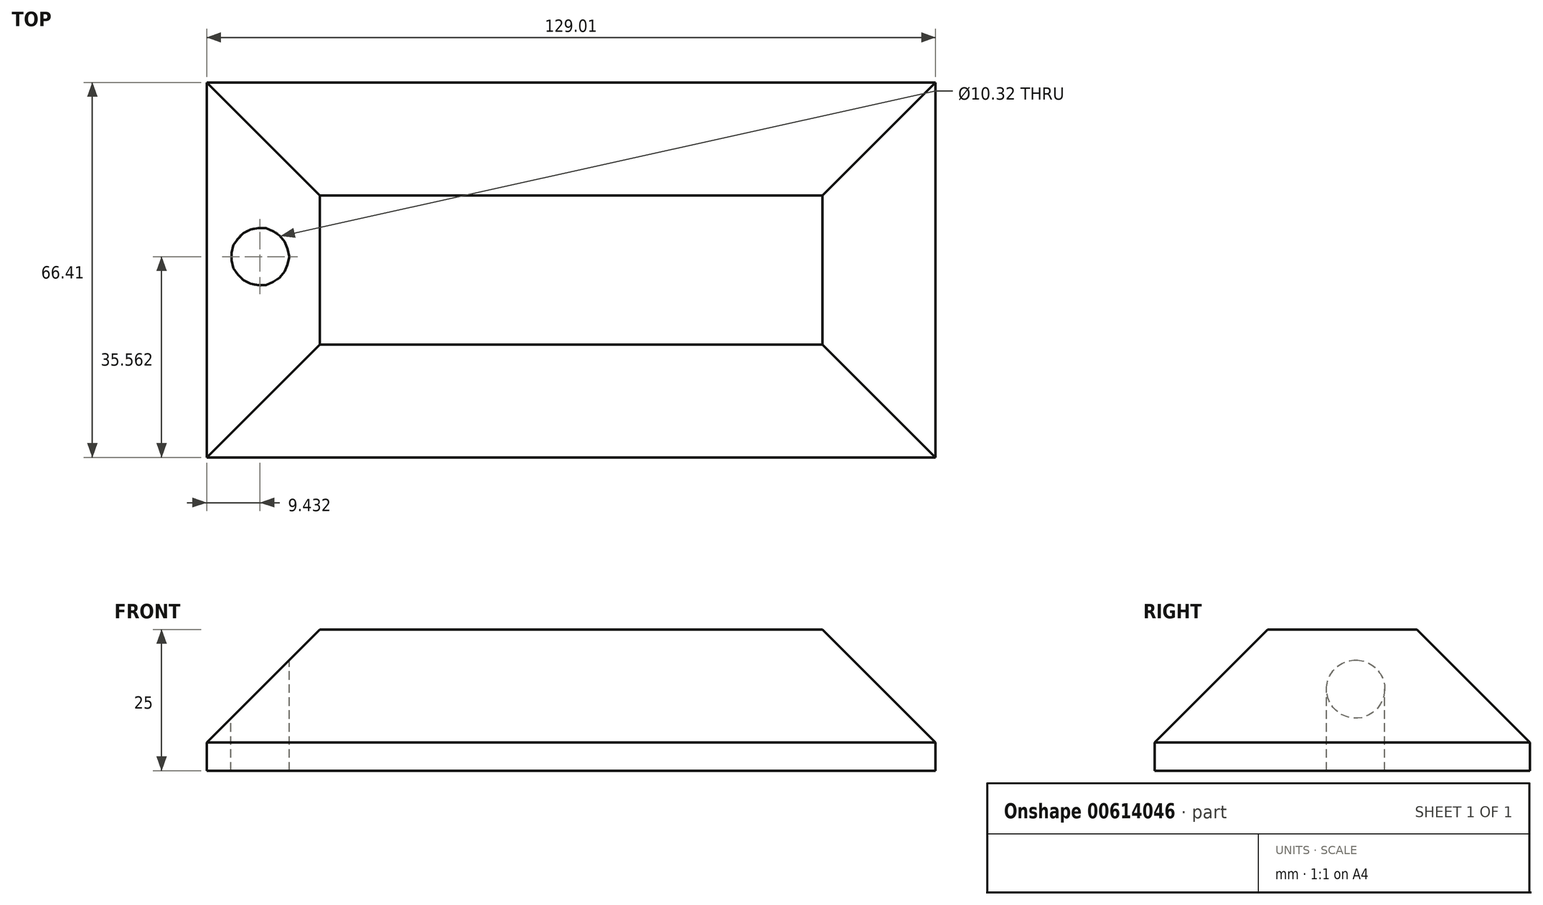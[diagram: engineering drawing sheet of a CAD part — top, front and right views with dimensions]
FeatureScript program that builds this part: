
annotation { "Feature Type Name" : "Feature", "Feature Type Description" : "" }
export const myFeature = defineFeature(function(context is Context, id is Id, definition is map)
    precondition{}
    {
        {
            var Q0;
            Q0=qCreatedBy(makeId("Top.planeOp"),FACE);
            var sketch = newSketch(context, id + "F0", { "sketchPlane" : qUnion([Q0])});
            skLineSegment(sketch, "E0.bottom", {"start": v(-62.87, 33.66) * mm, "end": v(66.14, 33.66) * mm});
            skLineSegment(sketch, "E0.top", {"start": v(-62.87, -32.75) * mm, "end": v(66.14, -32.75) * mm});
            skLineSegment(sketch, "E0.left", {"start": v(-62.87, 33.66) * mm, "end": v(-62.87, -32.75) * mm});
            skLineSegment(sketch, "E0.right", {"start": v(66.14, 33.66) * mm, "end": v(66.14, -32.75) * mm});
            skSolve(sketch);
        }
        {
            var Q0;
            Q0=makeQuery(id+"F0.imprint","IMPRINT",FACE,{"disambiguationData":[TD([[makeQuery(id+"F0.imprint","IMPRINT",EDGE,{"derivedFrom":sQuery(id+"F0.wireOp",EDGE,"E0.bottom")}),-1.0]])]});
            extrude(context, id + "F1", {"entities" : qUnion([Q0]), "depth" : 25 * mm, "offsetDistance" : 25 * mm});
        }
        {
            var Q0;
            Q0=makeQuery(id+"F1.opExtrude","CAP_FACE",FACE,{"disambiguationData":[OSD([sQuery(id+"F0.wireOp",EDGE,"E0.bottom"),sQuery(id+"F0.wireOp",EDGE,"E0.top"),sQuery(id+"F0.wireOp",EDGE,"E0.left"),sQuery(id+"F0.wireOp",EDGE,"E0.right")])],"isStart":false});
            var sketch = newSketch(context, id + "F2", { "sketchPlane" : qUnion([Q0])});
            skCircle(sketch, "E1", {"center": v(-53.44, 2.81) * mm, "radius": 5.16 * mm});
            skSolve(sketch);
        }
        {
            var Q0;
            Q0=makeQuery(id+"F2.imprint","IMPRINT",FACE,{"disambiguationData":[TD([[makeQuery(id+"F2.imprint","IMPRINT",EDGE,{"derivedFrom":sQuery(id+"F2.wireOp",EDGE,"E1")}),1.0]])]});
            extrude(context, id + "F3", {"entities" : qUnion([Q0]), "operationType" : NewBodyOperationType.REMOVE, "oppositeDirection" : true, "depth" : 25 * mm, "offsetDistance" : 25 * mm});
        }
        {
            var Q0;
            Q0=makeQuery(id+"F1.opExtrude","CAP_EDGE",EDGE,{"disambiguationData":[OSD([sQuery(id+"F0.wireOp",EDGE,"E0.top")])],"isStart":false});
            var Q1;
            Q1=makeQuery(id+"F1.opExtrude","CAP_EDGE",EDGE,{"disambiguationData":[OSD([sQuery(id+"F0.wireOp",EDGE,"E0.left")])],"isStart":false});
            var Q2;
            Q2=makeQuery(id+"F1.opExtrude","CAP_EDGE",EDGE,{"disambiguationData":[OSD([sQuery(id+"F0.wireOp",EDGE,"E0.bottom")])],"isStart":false});
            var Q3;
            Q3=makeQuery(id+"F1.opExtrude","CAP_EDGE",EDGE,{"disambiguationData":[OSD([sQuery(id+"F0.wireOp",EDGE,"E0.right")])],"isStart":false});
            chamfer(context, id + "F4", {"entities" : qUnion([Q0, Q1, Q2, Q3]), "width" : 20 * mm, "tangentPropagation" : true});
        }
    });
